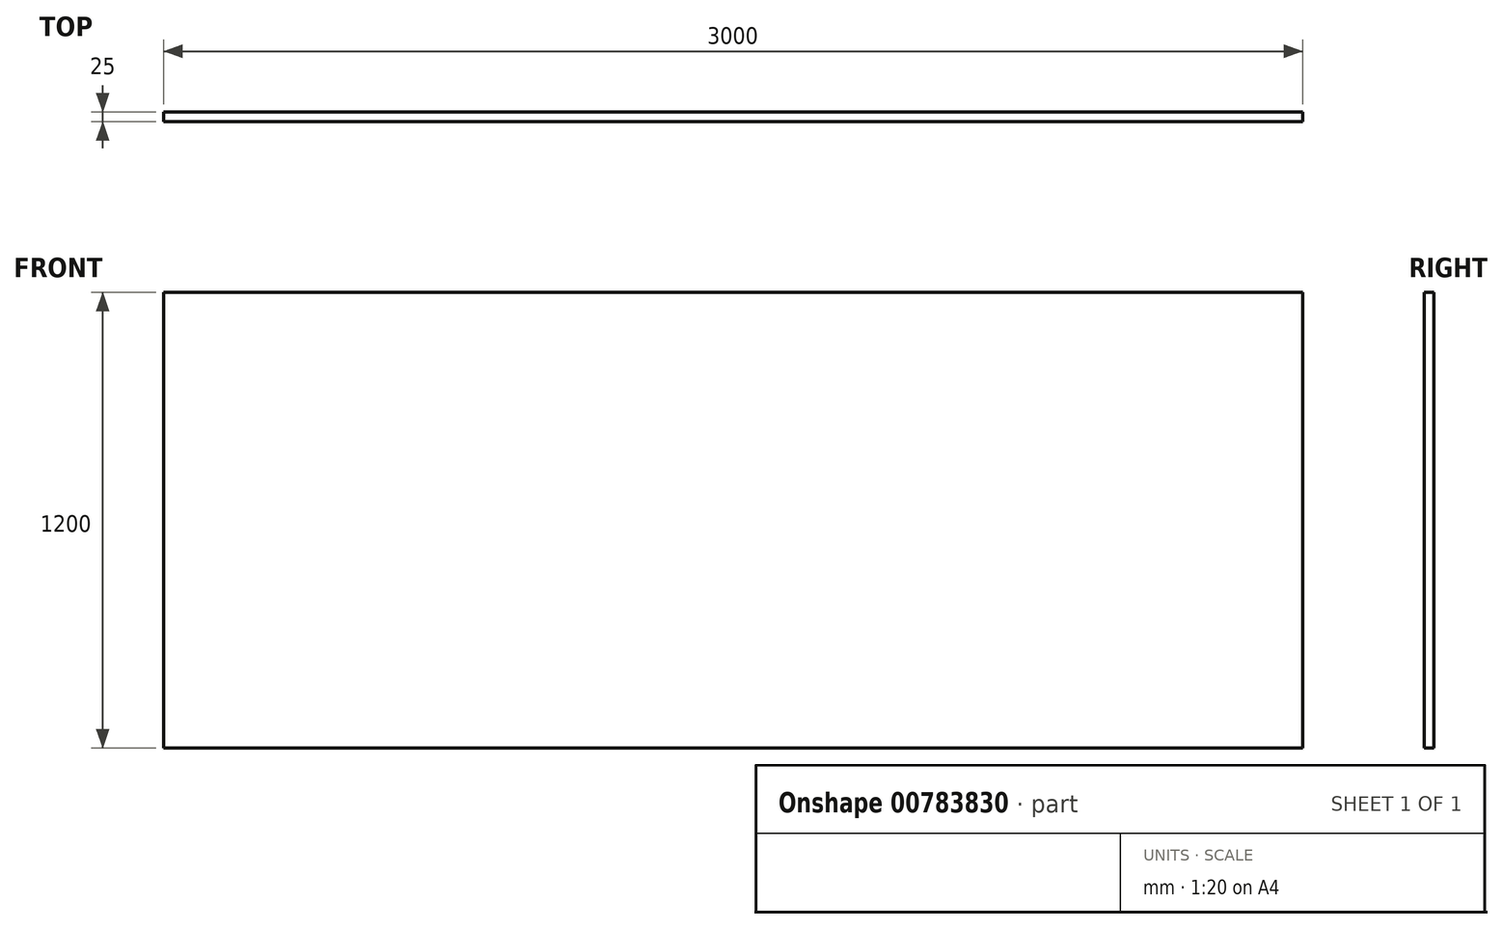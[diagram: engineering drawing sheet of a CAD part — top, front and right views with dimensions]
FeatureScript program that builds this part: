
annotation { "Feature Type Name" : "Feature", "Feature Type Description" : "" }
export const myFeature = defineFeature(function(context is Context, id is Id, definition is map)
    precondition{}
    {
        {
            var Q0;
            Q0=qCreatedBy(makeId("Front.planeOp"),FACE);
            var sketch = newSketch(context, id + "F0", { "sketchPlane" : qUnion([Q0])});
            skLineSegment(sketch, "E0.bottom", {"start": v(-93.9, 1163.02) * mm, "end": v(2906.1, 1163.02) * mm});
            skLineSegment(sketch, "E0.top", {"start": v(-93.9, -36.98) * mm, "end": v(2906.1, -36.98) * mm});
            skLineSegment(sketch, "E0.left", {"start": v(-93.9, 1163.02) * mm, "end": v(-93.9, -36.98) * mm});
            skLineSegment(sketch, "E0.right", {"start": v(2906.1, 1163.02) * mm, "end": v(2906.1, -36.98) * mm});
            skSolve(sketch);
        }
        {
            var Q0;
            Q0 = qSketchRegion(id + "F0", true);
            extrude(context, id + "F1", {"entities" : qUnion([Q0]), "depth" : 25 * mm, "offsetDistance" : 25 * mm});
        }
    });
